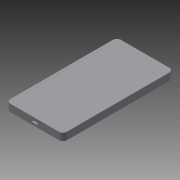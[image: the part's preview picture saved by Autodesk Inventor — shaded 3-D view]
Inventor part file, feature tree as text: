
AUTODESK INVENTOR PART (.ipt)
format: ipt  version: 2015 (Build 190159000, 159)  size: 128,512 bytes
history: native  units: mm
features: extrude x3, sketch x3, fillet x2
ambient origin geometry x8: Origin, YZ Plane, XZ Plane, XY Plane, X Axis, Y Axis, Z Axis, Center Point
bodies: Solid1 (feature_tree)
feature tree (8):
  extrude  "Extrusion1"  Depth=134.0mm
  extrude  "Extrusion2"  Depth=62.0mm
  extrude  "Extrusion3"  Depth=16.0mm
  fillet  "Fillet1"  Radius=16.5mm
  fillet  "Fillet2"  Radius=0.1mm
  sketch  "Sketch1"  dims[d0=68.8mm d1=134.0mm]
  sketch  "Sketch2"  dims[d2=9.3mm d3=0.0mm d4=62.0mm]
  sketch  "Sketch3"  dims[d5=3.4mm d6=16.0mm d7=16.5mm d8=0.1mm d9=0.0mm d10=7.2mm d11=2.1mm d12=30.8mm d13=5.0mm d14=0.0mm d15=5.0mm d16=0.5mm]
